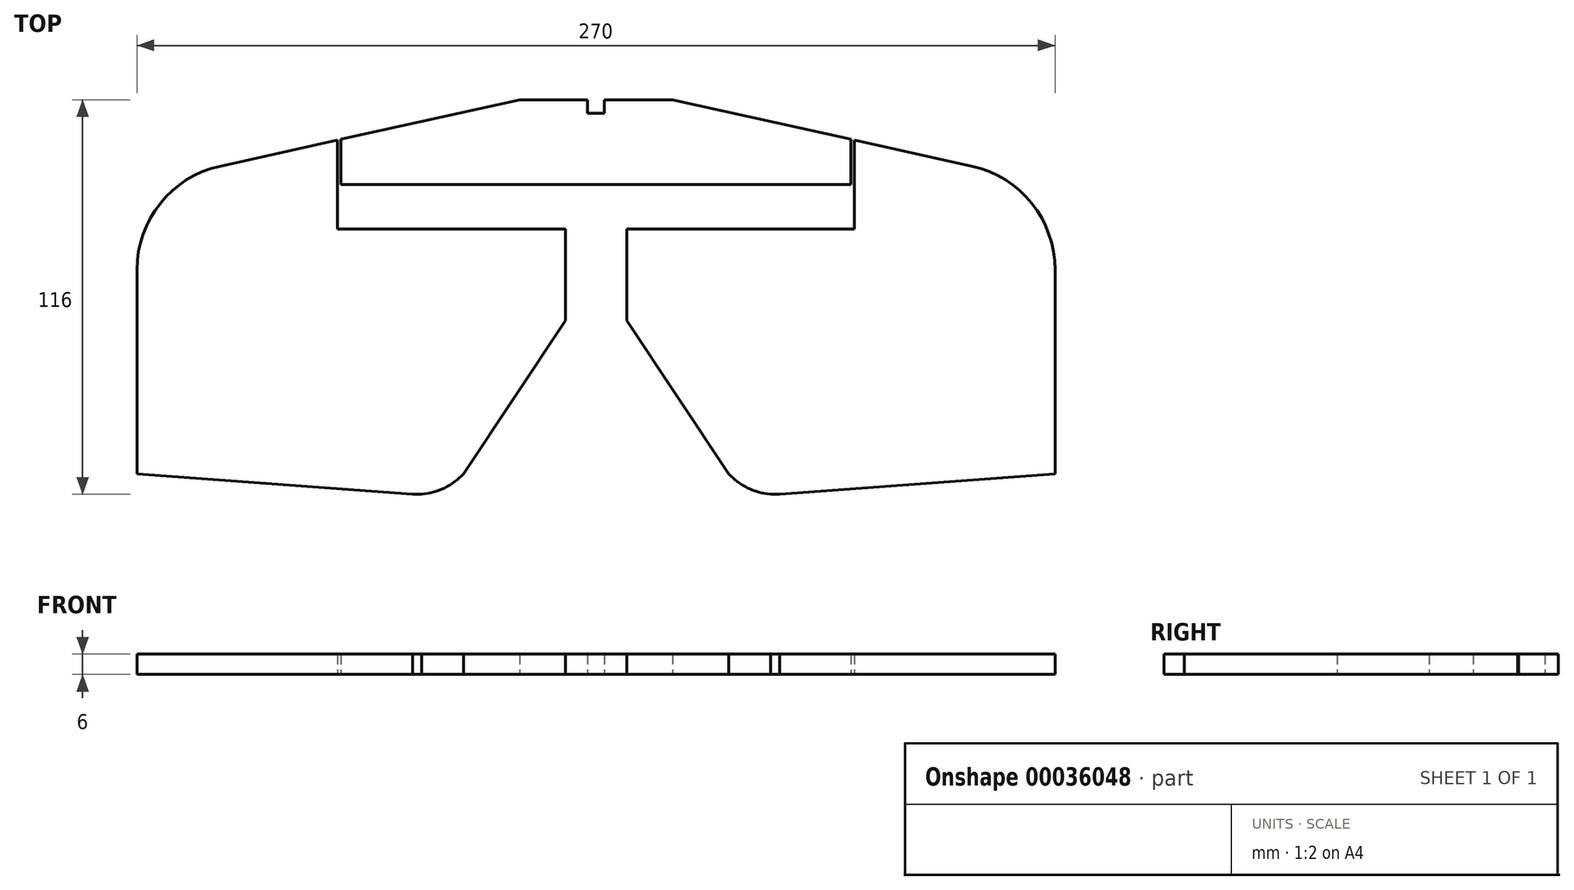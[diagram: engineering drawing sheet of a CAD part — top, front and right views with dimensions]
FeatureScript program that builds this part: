
annotation { "Feature Type Name" : "Feature", "Feature Type Description" : "" }
export const myFeature = defineFeature(function(context is Context, id is Id, definition is map)
    precondition{}
    {
        {
            var Q0;
            Q0=qCreatedBy(makeId("Top.planeOp"),FACE);
            var sketch = newSketch(context, id + "F0", { "sketchPlane" : qUnion([Q0])});
            skLineSegment(sketch, "E0.rect.bottom", {"start": v(135, -71.93) * mm, "end": v(-135, -71.93) * mm});
            skLineSegment(sketch, "E0.rect.top", {"start": v(135, 71.93) * mm, "end": v(-135, 71.93) * mm});
            skLineSegment(sketch, "E0.rect.left", {"start": v(135, -71.93) * mm, "end": v(135, 71.93) * mm});
            skLineSegment(sketch, "E0.rect.right", {"start": v(-135, -71.93) * mm, "end": v(-135, 71.93) * mm});
            skPoint(sketch, "E0.rect.middle", {"position": v(0, 0) * mm});
            skLineSegment(sketch, "E1", {"start": v(0, 71.93) * mm, "end": v(2.5, 71.93) * mm});
            skLineSegment(sketch, "E2", {"start": v(2.5, 71.93) * mm, "end": v(2.5, 67.93) * mm});
            skLineSegment(sketch, "E3", {"start": v(2.5, 67.93) * mm, "end": v(-2.5, 67.93) * mm});
            skLineSegment(sketch, "E4", {"start": v(-2.5, 67.93) * mm, "end": v(-2.5, 71.93) * mm});
            skLineSegment(sketch, "E5", {"start": v(-2.5, 71.93) * mm, "end": v(0, 71.93) * mm});
            skLineSegment(sketch, "E6", {"start": v(0, 71.93) * mm, "end": v(75, 71.93) * mm});
            skLineSegment(sketch, "E7", {"start": v(0, 71.93) * mm, "end": v(-75, 71.93) * mm});
            skLineSegment(sketch, "E8", {"start": v(75, 71.93) * mm, "end": v(75, 33.93) * mm});
            skLineSegment(sketch, "E9", {"start": v(75, 33.93) * mm, "end": v(-75, 33.93) * mm});
            skLineSegment(sketch, "E10", {"start": v(-75, 33.93) * mm, "end": v(-75, 71.93) * mm});
            skLineSegment(sketch, "E11", {"start": v(-135, 71.93) * mm, "end": v(-135, 46.93) * mm});
            skLineSegment(sketch, "E12", {"start": v(-135, 46.93) * mm, "end": v(135, 46.93) * mm});
            skLineSegment(sketch, "E13.rect.bottom", {"start": v(22.5, 62.93) * mm, "end": v(-22.5, 62.93) * mm});
            skLineSegment(sketch, "E13.rect.top", {"start": v(22.5, 80.94) * mm, "end": v(-22.5, 80.94) * mm});
            skLineSegment(sketch, "E13.rect.left", {"start": v(22.5, 62.93) * mm, "end": v(22.5, 80.94) * mm});
            skLineSegment(sketch, "E13.rect.right", {"start": v(-22.5, 62.93) * mm, "end": v(-22.5, 80.94) * mm});
            skPoint(sketch, "E13.rect.middle", {"position": v(0, 71.93) * mm});
            skLineSegment(sketch, "E14", {"start": v(135, 46.93) * mm, "end": v(22.5, 71.93) * mm});
            skLineSegment(sketch, "E15", {"start": v(-135, 46.93) * mm, "end": v(-22.5, 71.93) * mm});
            skLineSegment(sketch, "E16", {"start": v(0, 33.93) * mm, "end": v(9, 33.93) * mm});
            skLineSegment(sketch, "E17", {"start": v(9, 33.93) * mm, "end": v(9, 18.93) * mm});
            skLineSegment(sketch, "E18", {"start": v(9, 18.93) * mm, "end": v(-9, 18.93) * mm});
            skLineSegment(sketch, "E19", {"start": v(-9, 18.93) * mm, "end": v(-9, 33.93) * mm});
            skLineSegment(sketch, "E20", {"start": v(-9, 33.93) * mm, "end": v(0, 33.93) * mm});
            skLineSegment(sketch, "E21", {"start": v(0, 33.93) * mm, "end": v(-9, 33.93) * mm});
            skLineSegment(sketch, "E22", {"start": v(9, 18.93) * mm, "end": v(9, 6.93) * mm});
            skLineSegment(sketch, "E23", {"start": v(-9, 18.93) * mm, "end": v(-9, 6.93) * mm});
            skLineSegment(sketch, "E24.bottom", {"start": v(-9, 6.93) * mm, "end": v(-39, 6.93) * mm});
            skLineSegment(sketch, "E24.top", {"start": v(-9, -38.07) * mm, "end": v(-39, -38.07) * mm});
            skLineSegment(sketch, "E24.left", {"start": v(-9, 6.93) * mm, "end": v(-9, -38.07) * mm});
            skLineSegment(sketch, "E24.right", {"start": v(-39, 6.93) * mm, "end": v(-39, -38.07) * mm});
            skLineSegment(sketch, "E25.bottom", {"start": v(9, 6.93) * mm, "end": v(39, 6.93) * mm});
            skLineSegment(sketch, "E25.top", {"start": v(9, -38.07) * mm, "end": v(39, -38.07) * mm});
            skLineSegment(sketch, "E25.left", {"start": v(9, 6.93) * mm, "end": v(9, -38.07) * mm});
            skLineSegment(sketch, "E25.right", {"start": v(39, 6.93) * mm, "end": v(39, -38.07) * mm});
            skLineSegment(sketch, "E26", {"start": v(9, 6.93) * mm, "end": v(39, -38.07) * mm});
            skLineSegment(sketch, "E27", {"start": v(-9, 6.93) * mm, "end": v(-39, -38.07) * mm});
            skLineSegment(sketch, "E28.bottom", {"start": v(39, -38.07) * mm, "end": v(54, -38.07) * mm});
            skLineSegment(sketch, "E28.top", {"start": v(39, -44.07) * mm, "end": v(54, -44.07) * mm});
            skLineSegment(sketch, "E28.left", {"start": v(39, -38.07) * mm, "end": v(39, -44.07) * mm});
            skLineSegment(sketch, "E28.right", {"start": v(54, -38.07) * mm, "end": v(54, -44.07) * mm});
            skPoint(sketch, "E29.oppositeSnap0", {"position": v(46.5, -44.07) * mm});
            skLineSegment(sketch, "E29.bottom", {"start": v(-39, -38.07) * mm, "end": v(-54, -38.07) * mm});
            skLineSegment(sketch, "E29.top", {"start": v(-39, -44.07) * mm, "end": v(-54, -44.07) * mm});
            skLineSegment(sketch, "E29.left", {"start": v(-39, -38.07) * mm, "end": v(-39, -44.07) * mm});
            skLineSegment(sketch, "E29.right", {"start": v(-54, -38.07) * mm, "end": v(-54, -44.07) * mm});
            skLineSegment(sketch, "E30", {"start": v(-54, -38.07) * mm, "end": v(-135, -38.07) * mm});
            skLineSegment(sketch, "E31", {"start": v(54, -38.07) * mm, "end": v(135, -38.07) * mm});
            skLineSegment(sketch, "E32", {"start": v(54, -44.07) * mm, "end": v(135, -38.07) * mm});
            skLineSegment(sketch, "E33", {"start": v(-54, -44.07) * mm, "end": v(-135, -38.07) * mm});
            skArc(sketch, "E34", {"start": v(-54, -44.07) * mm, "mid": v(-45.8, -42.8) * mm, "end": v(-39, -38.07) * mm});
            skArc(sketch, "E35", {"start": v(39, -38.07) * mm, "mid": v(45.8, -42.8) * mm, "end": v(54, -44.07) * mm});
            skLineSegment(sketch, "E36", {"start": v(135, 46.93) * mm, "end": v(110.6, 52.36) * mm});
            skLineSegment(sketch, "E37", {"start": v(-135, 46.93) * mm, "end": v(-110.6, 52.36) * mm});
            skLineSegment(sketch, "E38", {"start": v(135, 46.93) * mm, "end": v(135, 21.93) * mm});
            skLineSegment(sketch, "E39", {"start": v(-135, 46.93) * mm, "end": v(-135, 21.93) * mm});
            skArc(sketch, "E40", {"start": v(135, 21.93) * mm, "mid": v(128.14, 41.43) * mm, "end": v(110.6, 52.36) * mm});
            skArc(sketch, "E41", {"start": v(-110.6, 52.36) * mm, "mid": v(-128.14, 41.43) * mm, "end": v(-135, 21.93) * mm});
            skLineSegment(sketch, "E42", {"start": v(-75, 33.93) * mm, "end": v(-76, 33.93) * mm});
            skLineSegment(sketch, "E43", {"start": v(-76, 33.93) * mm, "end": v(-76, 71.93) * mm});
            skLineSegment(sketch, "E44", {"start": v(75, 33.93) * mm, "end": v(76, 33.93) * mm});
            skLineSegment(sketch, "E45", {"start": v(76, 33.93) * mm, "end": v(76, 71.93) * mm});
            skSolve(sketch);
        }
        {
            var Q0;
            {var subQ0=sQuery(id+"F0.wireOp",EDGE,"E19");Q0=makeQuery(id+"F0.imprint","IMPRINT",FACE,{"disambiguationData":[TD([[makeQuery(id+"F0.imprint","IMPRINT",EDGE,{"derivedFrom":subQ0}),1.0]])]});}
            var Q1;
            Q1=makeQuery(id+"F0.imprint","IMPRINT",FACE,{"disambiguationData":[TD([[makeQuery(id+"F0.imprint","IMPRINT",EDGE,{"derivedFrom":sQuery(id+"F0.wireOp",EDGE,"E24.bottom")}),1.0]])]});
            var Q2;
            Q2=makeQuery(id+"F0.imprint","IMPRINT",FACE,{"disambiguationData":[TD([[makeQuery(id+"F0.imprint","IMPRINT",EDGE,{"derivedFrom":sQuery(id+"F0.wireOp",EDGE,"E25.bottom")}),-1.0]])]});
            var Q3;
            {var subQ7=sQuery(id+"F0.wireOp",EDGE,"E17");Q3=makeQuery(id+"F0.imprint","IMPRINT",FACE,{"disambiguationData":[TD([[makeQuery(id+"F0.imprint","IMPRINT",EDGE,{"derivedFrom":subQ7}),1.0]])]});}
            var Q4;
            {var subQ3=sQuery(id+"F0.wireOp",EDGE,"E29.bottom");Q4=makeQuery(id+"F0.imprint","IMPRINT",FACE,{"disambiguationData":[TD([[makeQuery(id+"F0.imprint","IMPRINT",EDGE,{"derivedFrom":subQ3}),1.0]])]});}
            var Q5;
            Q5=makeQuery(id+"F0.imprint","IMPRINT",FACE,{"disambiguationData":[TD([[makeQuery(id+"F0.imprint","IMPRINT",EDGE,{"derivedFrom":sQuery(id+"F0.wireOp",EDGE,"E29.right")}),-1.0]])]});
            var Q6;
            {var subQ4=sQuery(id+"F0.wireOp",EDGE,"E28.bottom");Q6=makeQuery(id+"F0.imprint","IMPRINT",FACE,{"disambiguationData":[TD([[makeQuery(id+"F0.imprint","IMPRINT",EDGE,{"derivedFrom":subQ4}),-1.0]])]});}
            var Q7;
            Q7=makeQuery(id+"F0.imprint","IMPRINT",FACE,{"disambiguationData":[TD([[makeQuery(id+"F0.imprint","IMPRINT",EDGE,{"derivedFrom":sQuery(id+"F0.wireOp",EDGE,"E28.right")}),1.0]])]});
            var Q8;
            {var subQ1=sQuery(id+"F0.wireOp",EDGE,"E16");Q8=makeQuery(id+"F0.imprint","IMPRINT",FACE,{"disambiguationData":[TD([[makeQuery(id+"F0.imprint","IMPRINT",EDGE,{"derivedFrom":subQ1}),1.0]])]});}
            var Q9;
            {var subQ7=sQuery(id+"F0.wireOp",EDGE,"E2");Q9=makeQuery(id+"F0.imprint","IMPRINT",FACE,{"disambiguationData":[TD([[makeQuery(id+"F0.imprint","IMPRINT",EDGE,{"derivedFrom":subQ7}),1.0]])]});}
            var Q10;
            {var subQ3=sQuery(id+"F0.wireOp",EDGE,"E12");var subQ5=sQuery(id+"F0.wireOp",EDGE,"E41");var subQ7=makeQuery(id+"F0.imprint","INTERSECT",VERTEX,{"derivedFrom":[subQ3,subQ5]});Q10=makeQuery(id+"F0.imprint","IMPRINT",FACE,{"disambiguationData":[TD([[makeQuery(id+"F0.imprint","IMPRINT",EDGE,{"disambiguationData":[TD([[subQ7,-1.0]])],"derivedFrom":subQ3}),1.0]])]});}
            var Q11;
            {var subQ0=sQuery(id+"F0.wireOp",EDGE,"E45");var subQ3=sQuery(id+"F0.wireOp",EDGE,"E12");var subQ4=makeQuery(id+"F0.imprint","INTERSECT",VERTEX,{"derivedFrom":[subQ3,subQ0]});Q11=makeQuery(id+"F0.imprint","IMPRINT",FACE,{"disambiguationData":[TD([[makeQuery(id+"F0.imprint","IMPRINT",EDGE,{"disambiguationData":[TD([[subQ4,-1.0]])],"derivedFrom":subQ3}),1.0]])]});}
            var Q12;
            {var subQ10=sQuery(id+"F0.wireOp",EDGE,"E13.rect.bottom");Q12=makeQuery(id+"F0.imprint","IMPRINT",FACE,{"disambiguationData":[TD([[makeQuery(id+"F0.imprint","IMPRINT",EDGE,{"derivedFrom":subQ10}),1.0]])]});}
            var Q13;
            Q13=makeQuery(id+"F0.imprint","IMPRINT",FACE,{"disambiguationData":[TD([[makeQuery(id+"F0.imprint","IMPRINT",EDGE,{"derivedFrom":sQuery(id+"F0.wireOp",EDGE,"E16")}),-1.0]])]});
            extrude(context, id + "F1", {"entities" : qUnion([Q0, Q1, Q2, Q3, Q4, Q5, Q6, Q7, Q8, Q9, Q10, Q11, Q12, Q13]), "depth" : 6 * mm});
        }
    });
